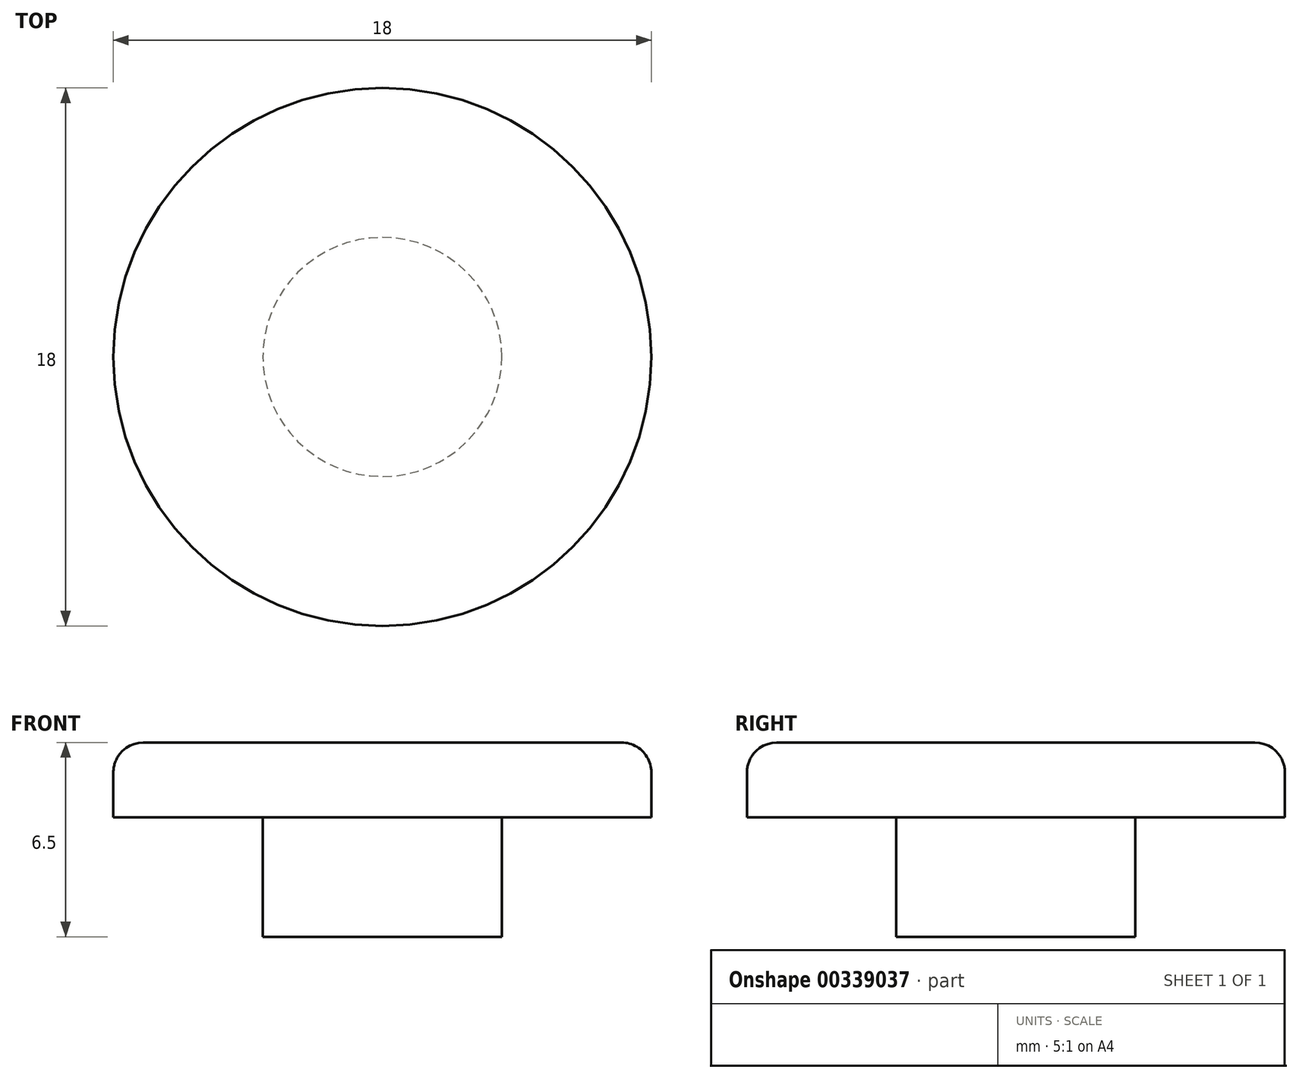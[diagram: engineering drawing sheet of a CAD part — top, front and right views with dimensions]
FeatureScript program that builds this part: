
annotation { "Feature Type Name" : "Feature", "Feature Type Description" : "" }
export const myFeature = defineFeature(function(context is Context, id is Id, definition is map)
    precondition{}
    {
        {
            var Q0;
            Q0=qCreatedBy(makeId("Top.planeOp"),FACE);
            var sketch = newSketch(context, id + "F0", { "sketchPlane" : qUnion([Q0])});
            skCircle(sketch, "E0", {"center": v(0, 0) * mm, "radius": 4 * mm});
            skSolve(sketch);
        }
        {
            var Q0;
            Q0 = qSketchRegion(id + "F0", true);
            extrude(context, id + "F1", {"entities" : qUnion([Q0]), "depth" : 4 * mm, "offsetDistance" : 25 * mm});
        }
        {
            var Q0;
            Q0=makeQuery(id+"F1.opExtrude","CAP_FACE",FACE,{"disambiguationData":[OSD([sQuery(id+"F0.wireOp",EDGE,"E0")])],"isStart":false});
            var sketch = newSketch(context, id + "F2", { "sketchPlane" : qUnion([Q0])});
            skCircle(sketch, "E1", {"center": v(0, 0) * mm, "radius": 9 * mm});
            skSolve(sketch);
        }
        {
            var Q0;
            Q0 = qSketchRegion(id + "F2", true);
            extrude(context, id + "F3", {"entities" : qUnion([Q0]), "operationType" : NewBodyOperationType.ADD, "depth" : 2.5 * mm, "offsetDistance" : 25 * mm});
        }
        {
            var Q0;
            Q0=makeQuery(id+"F3.opExtrude","CAP_EDGE",EDGE,{"disambiguationData":[OSD([sQuery(id+"F2.wireOp",EDGE,"E1")])],"isStart":false});
            fillet(context, id + "F4", {"entities" : qUnion([Q0]), "radius" : 1 * mm, "tangentPropagation" : true, "allowEdgeOverflow" : false});
        }
    });
